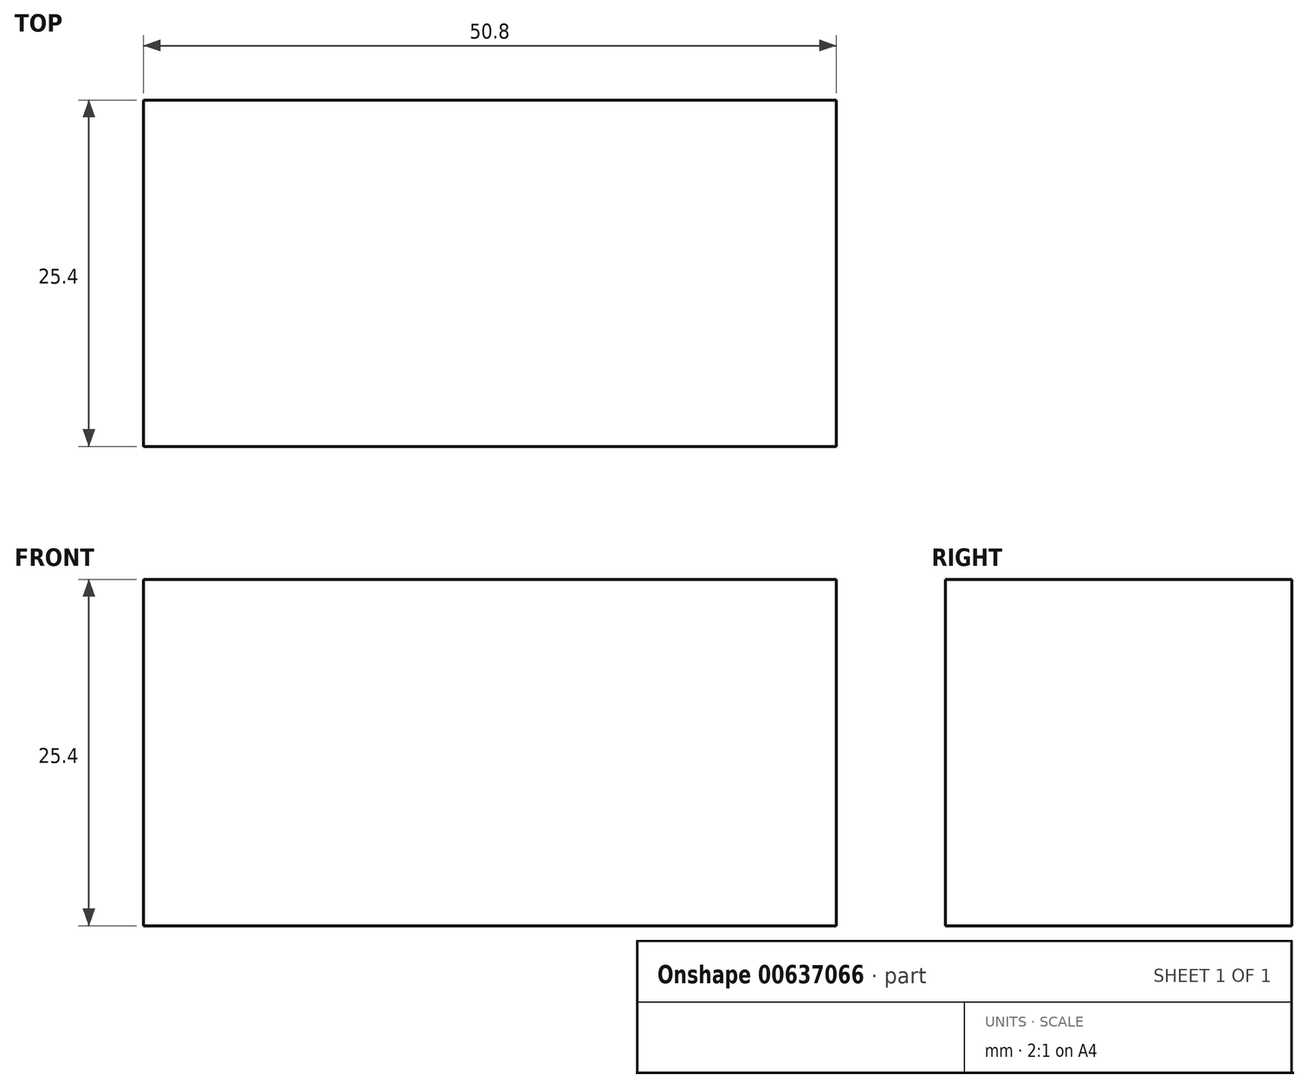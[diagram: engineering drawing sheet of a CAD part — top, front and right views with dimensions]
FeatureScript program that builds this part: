
annotation { "Feature Type Name" : "Feature", "Feature Type Description" : "" }
export const myFeature = defineFeature(function(context is Context, id is Id, definition is map)
    precondition{}
    {
        {
            var Q0;
            Q0=qCreatedBy(makeId("Front.planeOp"),FACE);
            var sketch = newSketch(context, id + "F0", { "sketchPlane" : qUnion([Q0])});
            skLineSegment(sketch, "E0.bottom", {"start": v(0, 0) * mm, "end": v(-50.8, 0) * mm});
            skLineSegment(sketch, "E0.top", {"start": v(0, 25.4) * mm, "end": v(-50.8, 25.4) * mm});
            skLineSegment(sketch, "E0.left", {"start": v(0, 0) * mm, "end": v(0, 25.4) * mm});
            skLineSegment(sketch, "E0.right", {"start": v(-50.8, 0) * mm, "end": v(-50.8, 25.4) * mm});
            skSolve(sketch);
        }
        {
            var Q0;
            Q0=makeQuery(id+"F0.imprint","IMPRINT",FACE,{"disambiguationData":[TD([[makeQuery(id+"F0.imprint","IMPRINT",EDGE,{"derivedFrom":sQuery(id+"F0.wireOp",EDGE,"E0.bottom")}),-1.0]])]});
            extrude(context, id + "F1", {"entities" : qUnion([Q0]), "depth" : 25.4 * mm, "offsetDistance" : 25.4 * mm});
        }
    });
